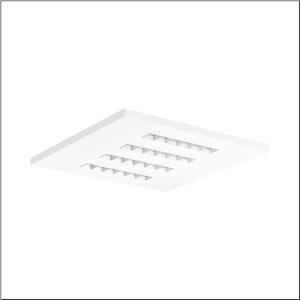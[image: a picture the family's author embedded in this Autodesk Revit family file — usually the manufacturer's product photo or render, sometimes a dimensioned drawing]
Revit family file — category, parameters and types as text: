
# Revit family: silica_r__21_square_51mx6mds34w_a914
name_source: partatom
category: Lighting Fixtures
units: mm (PartAtom-declared; Revit-internal decimal feet)

## family parameters
Cut with Voids When Loaded = No
Host = Face
Light Source = No
Part Type = Normal
Room Calculation Point = No
Round Connector Dimension = Use Diameter
Shared = No

## types (1)
- --- (1 x LED, 4600 lm, 29.2 W, 3000K)
    Apparent Load = 29 VA
    CIE Flux Codes = 83 98 100 100 100
    Color Rendering = 80
    Color Temperature = 3000K
    Default Elevation = 1800 mm
    Description = Silica® 21 Square, office luminaire, primary light control with lens, of PMMA, primary anti-glare with reflector, of PC, white, CAT 2 (L<= 3000cd/m²), light emission: direct distribution, primary light characteristic: symmetric, installation type: lay-in mounting, LED, rated luminous flux: 4.600lm, luminous efficacy: 158lm/W, light colour: 830, colour temperature: 3000K, control gear: DALI 2, with terminal, 5-pole, mains connection: 220..240V, AC, 50/60Hz, rated input power: 29.2W, luminaire housing, of sheet steel, coated, traffic white (RAL 9016), module: M600, length: 597mm, width: 597mm, height: 33mm, protection rating (complete): IP20, insulation class (complete): insulation class I (protective earthing), certification: CE, permissible operating ambient temperature: -20..+40°C, standard: EN 50419, packaging unit: 1 piece
    Height = 0 mm  [stored 0 ft]
    Lamp = 1 x LED
    Lamp Light Flux = 4600 lm
    Lamp Power = 29.2 W
    Lamp count = 1
    Length = 597 mm
    Luminous efficacy = 158 lm/W
    Manufacturer = Siteco
    ModVariant = No
    Model = 51MX6MDS34W
    Mounting Place = Ceiling
    Mounting Type = Recessed
    Number of Poles = 1
    OnlyDefault = Yes
    Power Factor = 1
    Product Name = Silica® 21 Square
    Product group = office luminaire | ceiling recessed
    ProductGroupID = 401
    Protection Class = Protection class I
    Protection Degree = IP 20
    RLX_Detail_Level = 1
    RLX_Emergency_Light_Flux = 0 lm
    RLX_Emergency_Type = 0
    RLX_Emergency_Type_DB = No
    RlxData = <blob elided: 37597 chars, md5=80722ef3>
    Socket = socket
    Standby Power = 0 W
    System Light Flux = 4600 lm
    System Power = 29 W
    Type Comments = factory setting: luminous flux: 100 % | dim-lin: 254 | 393 mA
    Type Image = l_1275220.jpg
    URL = http://relux.com
    VarID = @adj_078950
    Voltage = 0 V
    Weight = 0.00 kg
    Width = 597 mm

note: [stored X ft] marks values corroborated as IEEE doubles in the binary element streams (Revit-internal decimal feet)

## geometry (parser evidence)
native form markers: Blend x4, Sweep x10
no freeform markers — native parametric forms only
